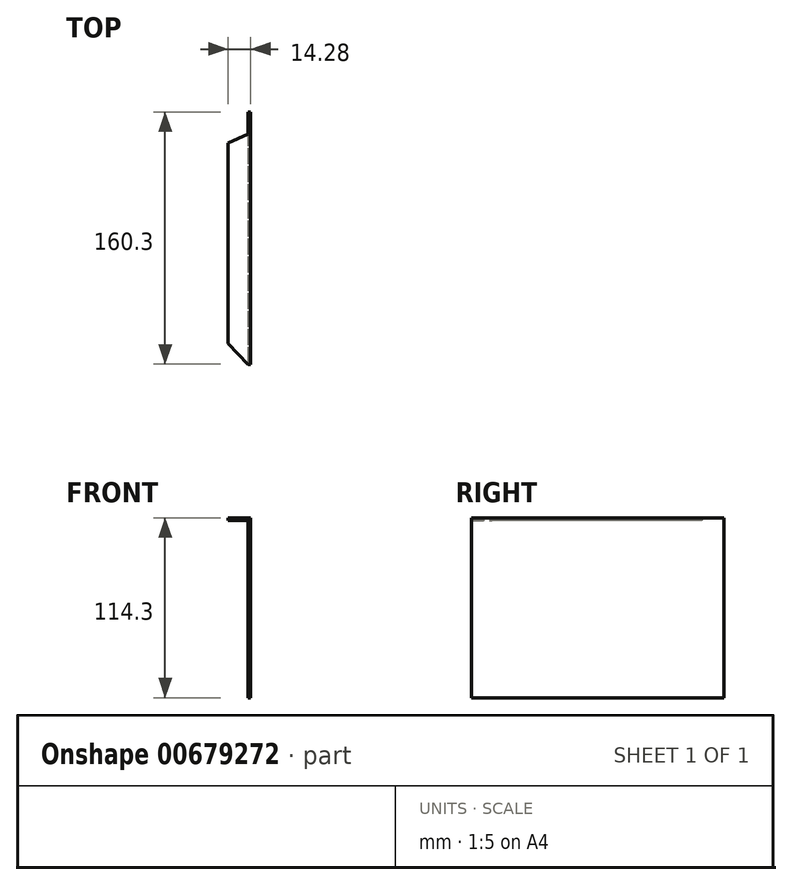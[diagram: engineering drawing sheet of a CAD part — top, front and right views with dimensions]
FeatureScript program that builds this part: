
annotation { "Feature Type Name" : "Feature", "Feature Type Description" : "" }
export const myFeature = defineFeature(function(context is Context, id is Id, definition is map)
    precondition{}
    {
        {
            var Q0;
            Q0=qCreatedBy(makeId("Top.planeOp"),FACE);
            var sketch = newSketch(context, id + "F0", { "sketchPlane" : qUnion([Q0])});
            skLineSegment(sketch, "E0.bottom", {"start": v(0.8, 80.15) * mm, "end": v(-0.8, 80.15) * mm});
            skLineSegment(sketch, "E0.top", {"start": v(0.8, -80.15) * mm, "end": v(-0.8, -80.15) * mm});
            skLineSegment(sketch, "E0.left", {"start": v(0.8, 80.15) * mm, "end": v(0.8, -80.15) * mm});
            skLineSegment(sketch, "E0.right", {"start": v(-0.8, 80.15) * mm, "end": v(-0.8, -80.15) * mm});
            skPoint(sketch, "E0.middle", {"position": v(0, 0) * mm});
            skLineSegment(sketch, "E1", {"start": v(-0.8, 80.15) * mm, "end": v(-0.8, 80.15) * mm});
            skLineSegment(sketch, "E2", {"start": v(-0.8, 80.15) * mm, "end": v(0.8, 80.15) * mm});
            skSolve(sketch);
        }
        {
            var Q0;
            Q0=qSketchRegion(id+"F0",true);
            extrude(context, id + "F1", {"entities" : qUnion([Q0]), "depth" : 114.3 * mm});
        }
        {
            var Q0;
            Q0=makeQuery(id+"F1.opExtrude","SWEPT_FACE",FACE,{"disambiguationData":[OSD([sQuery(id+"F0.wireOp",EDGE,"E0.right")])]});
            var sketch = newSketch(context, id + "F2", { "sketchPlane" : qUnion([Q0])});
            skPoint(sketch, "E3", {"position": v(-66, 114.3) * mm});
            skPoint(sketch, "E4", {"position": v(80.15, 114.3) * mm});
            skLineSegment(sketch, "E5.bottom", {"start": v(-66, 114.3) * mm, "end": v(80.15, 114.3) * mm});
            skLineSegment(sketch, "E5.top", {"start": v(-66, 112.71) * mm, "end": v(80.15, 112.71) * mm});
            skLineSegment(sketch, "E5.left", {"start": v(-66, 114.3) * mm, "end": v(-66, 112.71) * mm});
            skLineSegment(sketch, "E5.right", {"start": v(80.15, 114.3) * mm, "end": v(80.15, 112.71) * mm});
            skSolve(sketch);
        }
        {
            var Q0;
            Q0=qSketchRegion(id+"F2",true);
            extrude(context, id + "F3", {"entities" : qUnion([Q0]), "operationType" : NewBodyOperationType.ADD, "depth" : 12.7 * mm, "offsetDistance" : 25.4 * mm});
        }
        {
            var Q0;
            Q0=makeQuery(id+"F3.boolean.opBoolean","MERGE",FACE,{"derivedFrom":[makeQuery(id+"F1.opExtrude","CAP_FACE",FACE,{"disambiguationData":[OSD([sQuery(id+"F0.wireOp",EDGE,"E0.top"),sQuery(id+"F0.wireOp",EDGE,"E0.left"),sQuery(id+"F0.wireOp",EDGE,"E0.right"),sQuery(id+"F0.wireOp",EDGE,"E2")])],"isStart":false}),makeQuery(id+"F3.opExtrude","SWEPT_FACE",FACE,{"disambiguationData":[OSD([sQuery(id+"F2.wireOp",EDGE,"E5.bottom")])]})]});
            var sketch = newSketch(context, id + "F4", { "sketchPlane" : qUnion([Q0])});
            skLineSegment(sketch, "E6", {"start": v(-0.91, -80.15) * mm, "end": v(-13.5, -67.12) * mm});
            skLineSegment(sketch, "E7", {"start": v(-13.5, -67.12) * mm, "end": v(-13.5, -80.15) * mm});
            skLineSegment(sketch, "E8", {"start": v(-13.5, -80.15) * mm, "end": v(-0.91, -80.15) * mm});
            skLineSegment(sketch, "E9", {"start": v(-0.8, 66) * mm, "end": v(-13.5, 60.42) * mm});
            skLineSegment(sketch, "E10", {"start": v(-13.5, 60.42) * mm, "end": v(-13.5, 66) * mm});
            skLineSegment(sketch, "E11", {"start": v(-13.5, 66) * mm, "end": v(-0.8, 66) * mm});
            skSolve(sketch);
        }
        {
            var Q0;
            Q0 = qSketchRegion(id + "F4", true);
            extrude(context, id + "F5", {"entities" : qUnion([Q0]), "operationType" : NewBodyOperationType.REMOVE, "oppositeDirection" : true, "depth" : 25.4 * mm, "offsetDistance" : 25.4 * mm});
        }
    });
